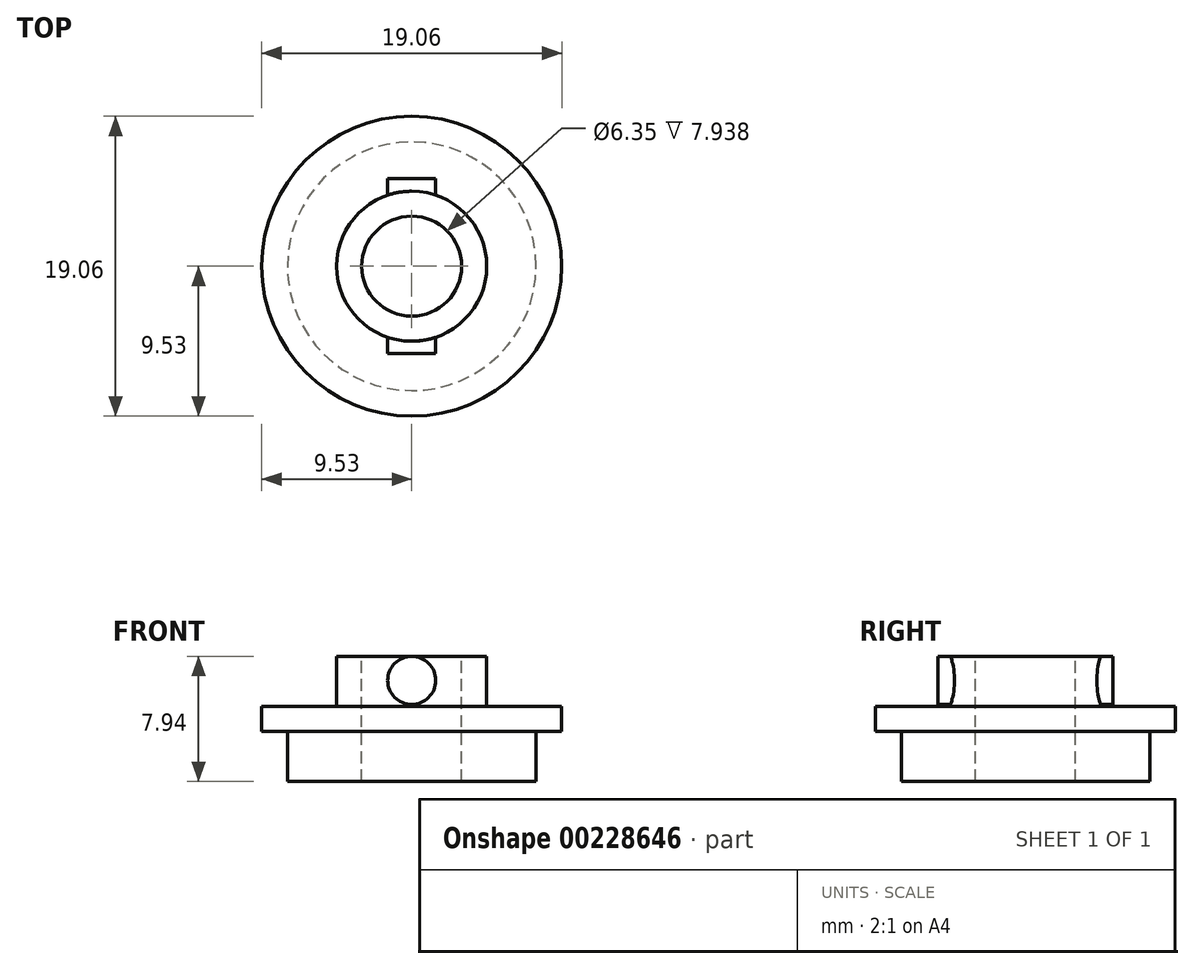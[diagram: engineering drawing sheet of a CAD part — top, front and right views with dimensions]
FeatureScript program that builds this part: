
annotation { "Feature Type Name" : "Feature", "Feature Type Description" : "" }
export const myFeature = defineFeature(function(context is Context, id is Id, definition is map)
    precondition{}
    {
        {
            var Q0;
            Q0=qCreatedBy(makeId("Top.planeOp"),FACE);
            var sketch = newSketch(context, id + "F0", { "sketchPlane" : qUnion([Q0])});
            skCircle(sketch, "E0", {"center": v(0, 0) * mm, "radius": 7.9 * mm});
            skSolve(sketch);
        }
        {
            var Q0;
            Q0 = qSketchRegion(id + "F0", true);
            extrude(context, id + "F1", {"entities" : qUnion([Q0]), "depth" : 3.17 * mm});
        }
        {
            var Q0;
            Q0=makeQuery(id+"F1.opExtrude","CAP_FACE",FACE,{"disambiguationData":[OSD([sQuery(id+"F0.wireOp",EDGE,"E0")])],"isStart":false});
            var sketch = newSketch(context, id + "F2", { "sketchPlane" : qUnion([Q0])});
            skCircle(sketch, "E1", {"center": v(0, 0) * mm, "radius": 9.53 * mm});
            skSolve(sketch);
        }
        {
            var Q0;
            Q0 = qSketchRegion(id + "F2", true);
            extrude(context, id + "F3", {"entities" : qUnion([Q0]), "operationType" : NewBodyOperationType.ADD, "depth" : 1.59 * mm});
        }
        {
            var Q0;
            Q0=makeQuery(id+"F3.opExtrude","CAP_FACE",FACE,{"disambiguationData":[OSD([sQuery(id+"F2.wireOp",EDGE,"E1")])],"isStart":false});
            var sketch = newSketch(context, id + "F4", { "sketchPlane" : qUnion([Q0])});
            skCircle(sketch, "E2", {"center": v(0, 0) * mm, "radius": 4.76 * mm});
            skSolve(sketch);
        }
        {
            var Q0;
            Q0 = qSketchRegion(id + "F4", true);
            extrude(context, id + "F5", {"entities" : qUnion([Q0]), "operationType" : NewBodyOperationType.ADD, "depth" : 3.17 * mm});
        }
        {
            var Q0;
            Q0=qCreatedBy(makeId("Front.planeOp"),FACE);
            var sketch = newSketch(context, id + "F6", { "sketchPlane" : qUnion([Q0])});
            skCircle(sketch, "E3", {"center": v(0, 6.41) * mm, "radius": 1.52 * mm});
            skSolve(sketch);
        }
        {
            var Q0;
            Q0 = qSketchRegion(id + "F6", true);
            extrude(context, id + "F7", {"entities" : qUnion([Q0]), "operationType" : NewBodyOperationType.ADD, "endBound" : BoundingType.SYMMETRIC, "depth" : 11.1 * mm});
        }
        {
            var Q0;
            Q0=makeQuery(id+"F5.opExtrude","CAP_FACE",FACE,{"disambiguationData":[OSD([sQuery(id+"F4.wireOp",EDGE,"E2")])],"isStart":false});
            var sketch = newSketch(context, id + "F8", { "sketchPlane" : qUnion([Q0])});
            skCircle(sketch, "E4", {"center": v(0, 0) * mm, "radius": 3.18 * mm});
            skSolve(sketch);
        }
        {
            var Q0;
            Q0 = qSketchRegion(id + "F8", true);
            extrude(context, id + "F9", {"entities" : qUnion([Q0]), "operationType" : NewBodyOperationType.REMOVE, "endBound" : BoundingType.UP_TO_NEXT, "oppositeDirection" : true, "depth" : 25.4 * mm});
        }
    });
